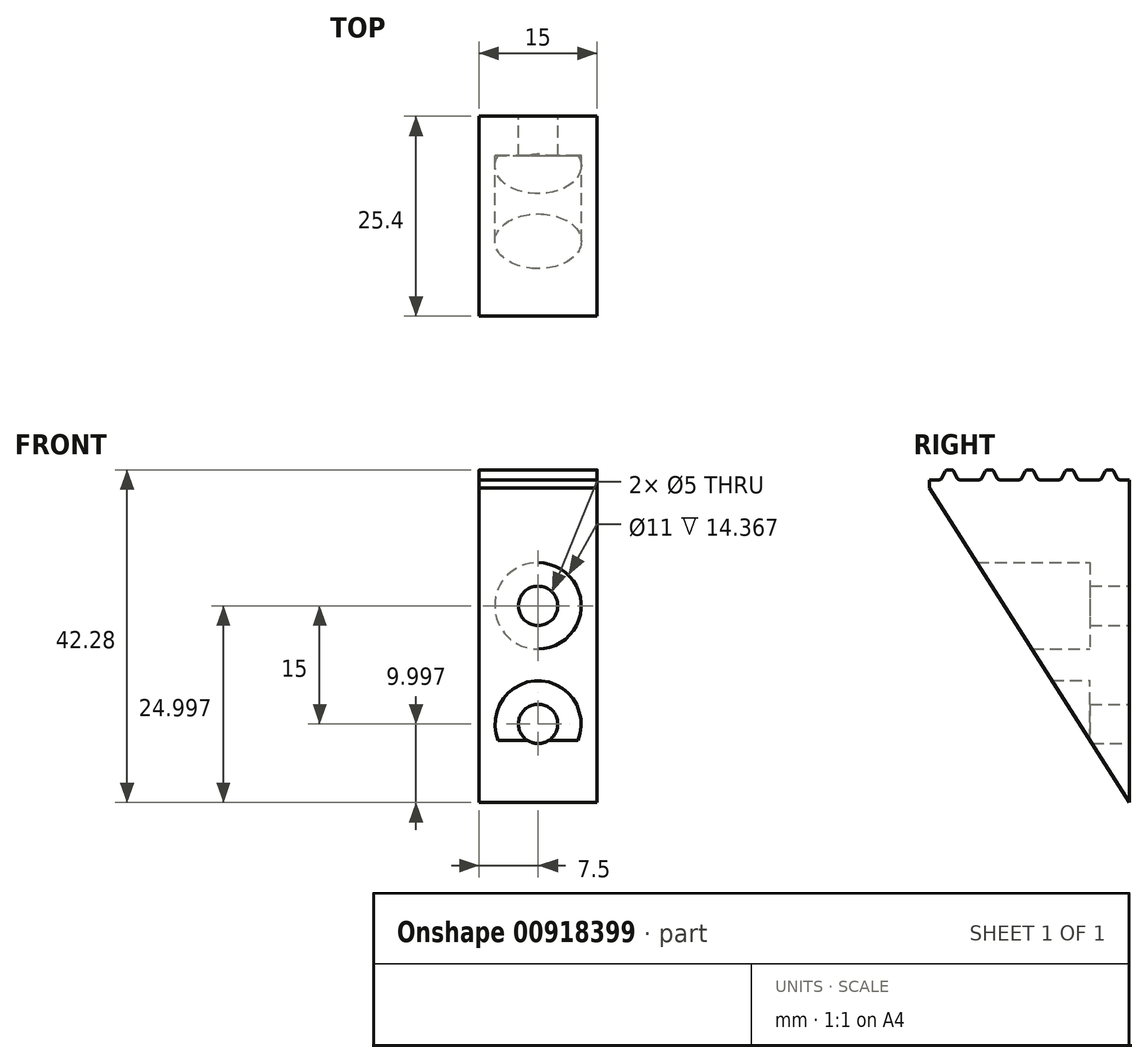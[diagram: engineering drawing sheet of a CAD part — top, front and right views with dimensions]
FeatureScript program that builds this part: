
annotation { "Feature Type Name" : "Feature", "Feature Type Description" : "" }
export const myFeature = defineFeature(function(context is Context, id is Id, definition is map)
    precondition{}
    {
        {
            var Q0;
            Q0=qCreatedBy(makeId("Right.planeOp"),FACE);
            var sketch = newSketch(context, id + "F0", { "sketchPlane" : qUnion([Q0])});
            skArc(sketch, "E0", {"start": v(8.88, -0.13) * mm, "mid": v(9.08, -0.07) * mm, "end": v(9.22, 0.1) * mm});
            skLineSegment(sketch, "E1", {"start": v(9.22, 0.1) * mm, "end": v(9.6, 0.92) * mm});
            skArc(sketch, "E2", {"start": v(9.95, 1.14) * mm, "mid": v(9.75, 1.08) * mm, "end": v(9.6, 0.92) * mm});
            skLineSegment(sketch, "E3", {"start": v(9.95, 1.14) * mm, "end": v(10.37, 1.14) * mm});
            skArc(sketch, "E4", {"start": v(10.7, 0.93) * mm, "mid": v(10.57, 1.08) * mm, "end": v(10.37, 1.14) * mm});
            skLineSegment(sketch, "E5", {"start": v(10.7, 0.93) * mm, "end": v(11.1, 0.1) * mm});
            skArc(sketch, "E6", {"start": v(11.1, 0.1) * mm, "mid": v(11.24, -0.07) * mm, "end": v(11.44, -0.13) * mm});
            skLineSegment(sketch, "E7", {"start": v(11.44, -0.13) * mm, "end": v(12.7, -0.13) * mm});
            skLineSegment(sketch, "E8", {"start": v(12.7, -0.13) * mm, "end": v(12.7, -1.14) * mm});
            skArc(sketch, "E9", {"start": v(3.8, -0.13) * mm, "mid": v(4, -0.07) * mm, "end": v(4.14, 0.1) * mm});
            skLineSegment(sketch, "E10", {"start": v(4.14, 0.1) * mm, "end": v(4.53, 0.92) * mm});
            skArc(sketch, "E11", {"start": v(4.87, 1.14) * mm, "mid": v(4.67, 1.08) * mm, "end": v(4.53, 0.92) * mm});
            skLineSegment(sketch, "E12", {"start": v(4.87, 1.14) * mm, "end": v(5.29, 1.14) * mm});
            skArc(sketch, "E13", {"start": v(5.63, 0.93) * mm, "mid": v(5.49, 1.08) * mm, "end": v(5.29, 1.14) * mm});
            skLineSegment(sketch, "E14", {"start": v(5.63, 0.93) * mm, "end": v(6.02, 0.1) * mm});
            skArc(sketch, "E15", {"start": v(6.02, 0.1) * mm, "mid": v(6.16, -0.07) * mm, "end": v(6.36, -0.13) * mm});
            skLineSegment(sketch, "E16", {"start": v(6.36, -0.13) * mm, "end": v(8.88, -0.13) * mm});
            skArc(sketch, "E17", {"start": v(-1.28, -0.13) * mm, "mid": v(-1.08, -0.07) * mm, "end": v(-0.94, 0.1) * mm});
            skLineSegment(sketch, "E18", {"start": v(-0.94, 0.1) * mm, "end": v(-0.55, 0.92) * mm});
            skArc(sketch, "E19", {"start": v(-0.2, 1.14) * mm, "mid": v(-0.41, 1.08) * mm, "end": v(-0.55, 0.92) * mm});
            skLineSegment(sketch, "E20", {"start": v(-0.2, 1.14) * mm, "end": v(0.2, 1.14) * mm});
            skArc(sketch, "E21", {"start": v(0.55, 0.93) * mm, "mid": v(0.4, 1.08) * mm, "end": v(0.2, 1.14) * mm});
            skLineSegment(sketch, "E22", {"start": v(0.55, 0.93) * mm, "end": v(0.94, 0.1) * mm});
            skArc(sketch, "E23", {"start": v(0.94, 0.1) * mm, "mid": v(1.08, -0.07) * mm, "end": v(1.28, -0.13) * mm});
            skLineSegment(sketch, "E24", {"start": v(1.28, -0.13) * mm, "end": v(3.8, -0.13) * mm});
            skArc(sketch, "E25", {"start": v(-6.36, -0.13) * mm, "mid": v(-6.16, -0.07) * mm, "end": v(-6.02, 0.1) * mm});
            skLineSegment(sketch, "E26", {"start": v(-6.02, 0.1) * mm, "end": v(-5.63, 0.92) * mm});
            skArc(sketch, "E27", {"start": v(-5.29, 1.14) * mm, "mid": v(-5.5, 1.08) * mm, "end": v(-5.63, 0.92) * mm});
            skLineSegment(sketch, "E28", {"start": v(-5.29, 1.14) * mm, "end": v(-4.87, 1.14) * mm});
            skArc(sketch, "E29", {"start": v(-4.53, 0.93) * mm, "mid": v(-4.67, 1.08) * mm, "end": v(-4.87, 1.14) * mm});
            skLineSegment(sketch, "E30", {"start": v(-4.53, 0.93) * mm, "end": v(-4.14, 0.1) * mm});
            skArc(sketch, "E31", {"start": v(-4.14, 0.1) * mm, "mid": v(-4, -0.07) * mm, "end": v(-3.8, -0.13) * mm});
            skLineSegment(sketch, "E32", {"start": v(-3.8, -0.13) * mm, "end": v(-1.28, -0.13) * mm});
            skLineSegment(sketch, "E33", {"start": v(-12.7, -0.13) * mm, "end": v(-11.44, -0.13) * mm});
            skArc(sketch, "E34", {"start": v(-11.44, -0.13) * mm, "mid": v(-11.24, -0.07) * mm, "end": v(-11.1, 0.1) * mm});
            skLineSegment(sketch, "E35", {"start": v(-11.1, 0.1) * mm, "end": v(-10.71, 0.92) * mm});
            skArc(sketch, "E36", {"start": v(-10.37, 1.14) * mm, "mid": v(-10.57, 1.08) * mm, "end": v(-10.71, 0.92) * mm});
            skLineSegment(sketch, "E37", {"start": v(-10.37, 1.14) * mm, "end": v(-9.95, 1.14) * mm});
            skArc(sketch, "E38", {"start": v(-9.61, 0.93) * mm, "mid": v(-9.75, 1.08) * mm, "end": v(-9.95, 1.14) * mm});
            skLineSegment(sketch, "E39", {"start": v(-9.61, 0.93) * mm, "end": v(-9.22, 0.1) * mm});
            skArc(sketch, "E40", {"start": v(-9.22, 0.1) * mm, "mid": v(-9.08, -0.07) * mm, "end": v(-8.88, -0.13) * mm});
            skLineSegment(sketch, "E41", {"start": v(-8.88, -0.13) * mm, "end": v(-6.36, -0.13) * mm});
            skLineSegment(sketch, "E42", {"start": v(12.7, -1.14) * mm, "end": v(-12.7, -1.14) * mm, "construction": true});
            skLineSegment(sketch, "E43", {"start": v(-12.7, -1.14) * mm, "end": v(-12.7, -0.13) * mm});
            skLineSegment(sketch, "E44.right", {"start": v(12.7, -1.14) * mm, "end": v(12.7, -41.14) * mm});
            skLineSegment(sketch, "E45", {"start": v(-12.7, -1.14) * mm, "end": v(12.7, -41.14) * mm});
            skSolve(sketch);
        }
        {
            var Q0;
            Q0=makeQuery(id+"F0.imprint","IMPRINT",FACE,{"disambiguationData":[TD([[makeQuery(id+"F0.imprint","IMPRINT",EDGE,{"derivedFrom":sQuery(id+"F0.wireOp",EDGE,"E0")}),-1.0]])]});
            extrude(context, id + "F1", {"entities" : qUnion([Q0]), "oppositeDirection" : true, "depth" : 7.5 * mm, "offsetDistance" : 25 * mm});
        }
        {
            var Q0;
            Q0=makeQuery(id+"F1.opExtrude","CAP_FACE",FACE,{"disambiguationData":[OSD([sQuery(id+"F0.wireOp",EDGE,"E0"),sQuery(id+"F0.wireOp",EDGE,"E1"),sQuery(id+"F0.wireOp",EDGE,"E2"),sQuery(id+"F0.wireOp",EDGE,"E3"),sQuery(id+"F0.wireOp",EDGE,"E4"),sQuery(id+"F0.wireOp",EDGE,"E5"),sQuery(id+"F0.wireOp",EDGE,"E6"),sQuery(id+"F0.wireOp",EDGE,"E7"),sQuery(id+"F0.wireOp",EDGE,"E8"),sQuery(id+"F0.wireOp",EDGE,"E9"),sQuery(id+"F0.wireOp",EDGE,"E10"),sQuery(id+"F0.wireOp",EDGE,"E11"),sQuery(id+"F0.wireOp",EDGE,"E12"),sQuery(id+"F0.wireOp",EDGE,"E13"),sQuery(id+"F0.wireOp",EDGE,"E14"),sQuery(id+"F0.wireOp",EDGE,"E15"),sQuery(id+"F0.wireOp",EDGE,"E16"),sQuery(id+"F0.wireOp",EDGE,"E17"),sQuery(id+"F0.wireOp",EDGE,"E18"),sQuery(id+"F0.wireOp",EDGE,"E19"),sQuery(id+"F0.wireOp",EDGE,"E20"),sQuery(id+"F0.wireOp",EDGE,"E21"),sQuery(id+"F0.wireOp",EDGE,"E22"),sQuery(id+"F0.wireOp",EDGE,"E23"),sQuery(id+"F0.wireOp",EDGE,"E24"),sQuery(id+"F0.wireOp",EDGE,"E25"),sQuery(id+"F0.wireOp",EDGE,"E26"),sQuery(id+"F0.wireOp",EDGE,"E27"),sQuery(id+"F0.wireOp",EDGE,"E28"),sQuery(id+"F0.wireOp",EDGE,"E29"),sQuery(id+"F0.wireOp",EDGE,"E30"),sQuery(id+"F0.wireOp",EDGE,"E31"),sQuery(id+"F0.wireOp",EDGE,"E32"),sQuery(id+"F0.wireOp",EDGE,"E33"),sQuery(id+"F0.wireOp",EDGE,"E34"),sQuery(id+"F0.wireOp",EDGE,"E35"),sQuery(id+"F0.wireOp",EDGE,"E36"),sQuery(id+"F0.wireOp",EDGE,"E37"),sQuery(id+"F0.wireOp",EDGE,"E38"),sQuery(id+"F0.wireOp",EDGE,"E39"),sQuery(id+"F0.wireOp",EDGE,"E40"),sQuery(id+"F0.wireOp",EDGE,"E41"),sQuery(id+"F0.wireOp",EDGE,"E43"),sQuery(id+"F0.wireOp",EDGE,"E44.right"),sQuery(id+"F0.wireOp",EDGE,"E45")])],"isStart":false});
            var sketch = newSketch(context, id + "F2", { "sketchPlane" : qUnion([Q0])});
            skLineSegment(sketch, "E46", {"start": v(-12.7, -0.13) * mm, "end": v(12.7, -0.13) * mm});
            skSolve(sketch);
        }
        {
            var Q0;
            Q0=makeQuery(id+"F1.opExtrude","SWEPT_BODY",BODY,{"disambiguationData":[OSD([sQuery(id+"F0.wireOp",EDGE,"E0"),sQuery(id+"F0.wireOp",EDGE,"E1"),sQuery(id+"F0.wireOp",EDGE,"E2"),sQuery(id+"F0.wireOp",EDGE,"E3"),sQuery(id+"F0.wireOp",EDGE,"E4"),sQuery(id+"F0.wireOp",EDGE,"E5"),sQuery(id+"F0.wireOp",EDGE,"E6"),sQuery(id+"F0.wireOp",EDGE,"E7"),sQuery(id+"F0.wireOp",EDGE,"E8"),sQuery(id+"F0.wireOp",EDGE,"E9"),sQuery(id+"F0.wireOp",EDGE,"E10"),sQuery(id+"F0.wireOp",EDGE,"E11"),sQuery(id+"F0.wireOp",EDGE,"E12"),sQuery(id+"F0.wireOp",EDGE,"E13"),sQuery(id+"F0.wireOp",EDGE,"E14"),sQuery(id+"F0.wireOp",EDGE,"E15"),sQuery(id+"F0.wireOp",EDGE,"E16"),sQuery(id+"F0.wireOp",EDGE,"E17"),sQuery(id+"F0.wireOp",EDGE,"E18"),sQuery(id+"F0.wireOp",EDGE,"E19"),sQuery(id+"F0.wireOp",EDGE,"E20"),sQuery(id+"F0.wireOp",EDGE,"E21"),sQuery(id+"F0.wireOp",EDGE,"E22"),sQuery(id+"F0.wireOp",EDGE,"E23"),sQuery(id+"F0.wireOp",EDGE,"E24"),sQuery(id+"F0.wireOp",EDGE,"E25"),sQuery(id+"F0.wireOp",EDGE,"E26"),sQuery(id+"F0.wireOp",EDGE,"E27"),sQuery(id+"F0.wireOp",EDGE,"E28"),sQuery(id+"F0.wireOp",EDGE,"E29"),sQuery(id+"F0.wireOp",EDGE,"E30"),sQuery(id+"F0.wireOp",EDGE,"E31"),sQuery(id+"F0.wireOp",EDGE,"E32"),sQuery(id+"F0.wireOp",EDGE,"E33"),sQuery(id+"F0.wireOp",EDGE,"E34"),sQuery(id+"F0.wireOp",EDGE,"E35"),sQuery(id+"F0.wireOp",EDGE,"E36"),sQuery(id+"F0.wireOp",EDGE,"E37"),sQuery(id+"F0.wireOp",EDGE,"E38"),sQuery(id+"F0.wireOp",EDGE,"E39"),sQuery(id+"F0.wireOp",EDGE,"E40"),sQuery(id+"F0.wireOp",EDGE,"E41"),sQuery(id+"F0.wireOp",EDGE,"E43"),sQuery(id+"F0.wireOp",EDGE,"E44.right"),sQuery(id+"F0.wireOp",EDGE,"E45")])]});
            var Q1;
            Q1=qCreatedBy(makeId("Right.planeOp"),FACE);
            mirror(context, id + "F4", {"operationType" : NewBodyOperationType.ADD, "entities" : qUnion([Q0]), "mirrorPlane" : qUnion([Q1])});
        }
        {
            var Q0;
            {var subQ0=makeQuery(id+"F3.boolean.opBoolean","MERGE",FACE,{"derivedFrom":[makeQuery(id+"F1.opExtrude","SWEPT_FACE",FACE,{"disambiguationData":[OSD([sQuery(id+"F0.wireOp",EDGE,"E7")])]}),makeQuery(id+"F1.opExtrude","SWEPT_FACE",FACE,{"disambiguationData":[OSD([sQuery(id+"F0.wireOp",EDGE,"E16")])]}),makeQuery(id+"F1.opExtrude","SWEPT_FACE",FACE,{"disambiguationData":[OSD([sQuery(id+"F0.wireOp",EDGE,"E24")])]}),makeQuery(id+"F1.opExtrude","SWEPT_FACE",FACE,{"disambiguationData":[OSD([sQuery(id+"F0.wireOp",EDGE,"E32")])]}),makeQuery(id+"F1.opExtrude","SWEPT_FACE",FACE,{"disambiguationData":[OSD([sQuery(id+"F0.wireOp",EDGE,"E33")])]}),makeQuery(id+"F1.opExtrude","SWEPT_FACE",FACE,{"disambiguationData":[OSD([sQuery(id+"F0.wireOp",EDGE,"E41")])]}),makeQuery(id+"F3.opExtrude","SWEPT_FACE",FACE,{"disambiguationData":[OSD([sQuery(id+"F2.wireOp",EDGE,"E46")])]})]});Q0=makeQuery(id+"F4.boolean.opBoolean","MERGE",FACE,{"derivedFrom":[subQ0,makeQuery(id+"F4.opPattern","COPY",FACE,{"derivedFrom":subQ0,"instanceName":"1"})]});}
            var sketch = newSketch(context, id + "F5", { "sketchPlane" : qUnion([Q0])});
            skCircle(sketch, "E47", {"center": v(10, 7.7) * mm, "radius": 0.8 * mm});
            skCircle(sketch, "E48", {"center": v(10, -7.7) * mm, "radius": 0.8 * mm});
            skCircle(sketch, "E49.MirrorC", {"center": v(-10, 7.7) * mm, "radius": 0.8 * mm});
            skCircle(sketch, "E50.MirrorC", {"center": v(-10, -7.7) * mm, "radius": 0.8 * mm});
            skSolve(sketch);
        }
        {
            var Q0;
            Q0=qSketchRegion(id+"F5",true);
            extrude(context, id + "F6", {"entities" : qUnion([Q0]), "operationType" : NewBodyOperationType.REMOVE, "oppositeDirection" : true, "depth" : 45 * mm, "offsetDistance" : 25 * mm});
        }
        {
            var Q0;
            {var subQ0=makeQuery(id+"F3.boolean.opBoolean","MERGE",FACE,{"derivedFrom":[makeQuery(id+"F1.opExtrude","SWEPT_FACE",FACE,{"disambiguationData":[OSD([sQuery(id+"F0.wireOp",EDGE,"E7")])]}),makeQuery(id+"F1.opExtrude","SWEPT_FACE",FACE,{"disambiguationData":[OSD([sQuery(id+"F0.wireOp",EDGE,"E16")])]}),makeQuery(id+"F1.opExtrude","SWEPT_FACE",FACE,{"disambiguationData":[OSD([sQuery(id+"F0.wireOp",EDGE,"E24")])]}),makeQuery(id+"F1.opExtrude","SWEPT_FACE",FACE,{"disambiguationData":[OSD([sQuery(id+"F0.wireOp",EDGE,"E32")])]}),makeQuery(id+"F1.opExtrude","SWEPT_FACE",FACE,{"disambiguationData":[OSD([sQuery(id+"F0.wireOp",EDGE,"E33")])]}),makeQuery(id+"F1.opExtrude","SWEPT_FACE",FACE,{"disambiguationData":[OSD([sQuery(id+"F0.wireOp",EDGE,"E41")])]}),makeQuery(id+"F3.opExtrude","SWEPT_FACE",FACE,{"disambiguationData":[OSD([sQuery(id+"F2.wireOp",EDGE,"E46")])]})]});Q0=makeQuery(id+"F4.boolean.opBoolean","MERGE",FACE,{"derivedFrom":[subQ0,makeQuery(id+"F4.opPattern","COPY",FACE,{"derivedFrom":subQ0,"instanceName":"1"})]});}
            var sketch = newSketch(context, id + "F7", { "sketchPlane" : qUnion([Q0])});
            skCircle(sketch, "E51.0", {"center": v(10, -7.7) * mm, "radius": 2 * mm});
            skCircle(sketch, "E52.0", {"center": v(10, 7.7) * mm, "radius": 2 * mm});
            skCircle(sketch, "E53.MirrorC", {"center": v(-10, 7.7) * mm, "radius": 2 * mm});
            skCircle(sketch, "E54.MirrorC", {"center": v(-10, -7.7) * mm, "radius": 2 * mm});
            skSolve(sketch);
        }
        {
            var Q0;
            Q0=qSketchRegion(id+"F7",true);
            var Q1;
            {var subQ0=sQuery(id+"F0.wireOp",EDGE,"E45");var subQ1=makeQuery(id+"F3.boolean.opBoolean","MERGE",FACE,{"derivedFrom":[makeQuery(id+"F1.opExtrude","SWEPT_FACE",FACE,{"disambiguationData":[OSD([subQ0])]}),makeQuery(id+"F3.opExtrude","SWEPT_FACE",FACE,{"disambiguationData":[OSD([subQ0])]})]});Q1=makeQuery(id+"F4.boolean.opBoolean","MERGE",FACE,{"derivedFrom":[subQ1,makeQuery(id+"F4.opPattern","COPY",FACE,{"derivedFrom":subQ1,"instanceName":"1"})]});}
            extrude(context, id + "F8", {"entities" : qUnion([Q0]), "operationType" : NewBodyOperationType.REMOVE, "endBound" : BoundingType.UP_TO_SURFACE, "oppositeDirection" : true, "depth" : 40 * mm, "endBoundEntityFace" : qUnion([Q1]), "offsetDistance" : 3 * mm, "hasSecondDirection" : true, "secondDirectionOppositeDirection" : true, "secondDirectionDepth" : 3 * mm});
        }
        {
            var Q0;
            {var subQ0=sQuery(id+"F0.wireOp",EDGE,"E44.right");var subQ1=sQuery(id+"F0.wireOp",EDGE,"E8");var subQ2=makeQuery(id+"F3.boolean.opBoolean","MERGE",FACE,{"derivedFrom":[makeQuery(id+"F1.opExtrude","SWEPT_FACE",FACE,{"disambiguationData":[OSD([subQ1,subQ0])]}),makeQuery(id+"F3.opExtrude","SWEPT_FACE",FACE,{"disambiguationData":[OSD([subQ1,subQ0])]})]});Q0=makeQuery(id+"F4.boolean.opBoolean","MERGE",FACE,{"derivedFrom":[subQ2,makeQuery(id+"F4.opPattern","COPY",FACE,{"derivedFrom":subQ2,"instanceName":"1"})]});}
            var sketch = newSketch(context, id + "F9", { "sketchPlane" : qUnion([Q0])});
            skCircle(sketch, "E55", {"center": v(0, -31.14) * mm, "radius": 2.5 * mm});
            skCircle(sketch, "E56", {"center": v(0, -16.14) * mm, "radius": 2.5 * mm});
            skSolve(sketch);
        }
        {
            var Q0;
            Q0=makeQuery(id+"F9.imprint","IMPRINT",FACE,{"disambiguationData":[TD([[makeQuery(id+"F9.imprint","IMPRINT",EDGE,{"derivedFrom":sQuery(id+"F9.wireOp",EDGE,"E55")}),1.0]])]});
            var Q1;
            Q1=makeQuery(id+"F9.imprint","IMPRINT",FACE,{"disambiguationData":[TD([[makeQuery(id+"F9.imprint","IMPRINT",EDGE,{"derivedFrom":sQuery(id+"F9.wireOp",EDGE,"E56")}),1.0]])]});
            var Q2;
            {var subQ0=sQuery(id+"F0.wireOp",EDGE,"E45");var subQ1=makeQuery(id+"F3.boolean.opBoolean","MERGE",FACE,{"derivedFrom":[makeQuery(id+"F1.opExtrude","SWEPT_FACE",FACE,{"disambiguationData":[OSD([subQ0])]}),makeQuery(id+"F3.opExtrude","SWEPT_FACE",FACE,{"disambiguationData":[OSD([subQ0])]})]});Q2=makeQuery(id+"F4.boolean.opBoolean","MERGE",FACE,{"derivedFrom":[subQ1,makeQuery(id+"F4.opPattern","COPY",FACE,{"derivedFrom":subQ1,"instanceName":"1"})]});}
            extrude(context, id + "F10", {"entities" : qUnion([Q0, Q1]), "operationType" : NewBodyOperationType.REMOVE, "endBound" : BoundingType.UP_TO_SURFACE, "oppositeDirection" : true, "depth" : 25 * mm, "endBoundEntityFace" : qUnion([Q2]), "offsetDistance" : 25 * mm});
        }
        {
            var Q0;
            {var subQ0=sQuery(id+"F0.wireOp",EDGE,"E44.right");var subQ1=sQuery(id+"F0.wireOp",EDGE,"E8");var subQ2=makeQuery(id+"F3.boolean.opBoolean","MERGE",FACE,{"derivedFrom":[makeQuery(id+"F1.opExtrude","SWEPT_FACE",FACE,{"disambiguationData":[OSD([subQ1,subQ0])]}),makeQuery(id+"F3.opExtrude","SWEPT_FACE",FACE,{"disambiguationData":[OSD([subQ1,subQ0])]})]});Q0=makeQuery(id+"F4.boolean.opBoolean","MERGE",FACE,{"derivedFrom":[subQ2,makeQuery(id+"F4.opPattern","COPY",FACE,{"derivedFrom":subQ2,"instanceName":"1"})]});}
            var sketch = newSketch(context, id + "F11", { "sketchPlane" : qUnion([Q0])});
            skCircle(sketch, "E57.0", {"center": v(0, -31.14) * mm, "radius": 5.5 * mm});
            skCircle(sketch, "E58.0", {"center": v(0, -16.14) * mm, "radius": 5.5 * mm});
            skSolve(sketch);
        }
        {
            var Q0;
            Q0=qSketchRegion(id+"F11",true);
            var Q1;
            {var subQ0=sQuery(id+"F0.wireOp",EDGE,"E45");var subQ1=makeQuery(id+"F3.boolean.opBoolean","MERGE",FACE,{"derivedFrom":[makeQuery(id+"F1.opExtrude","SWEPT_FACE",FACE,{"disambiguationData":[OSD([subQ0])]}),makeQuery(id+"F3.opExtrude","SWEPT_FACE",FACE,{"disambiguationData":[OSD([subQ0])]})]});Q1=makeQuery(id+"F4.boolean.opBoolean","MERGE",FACE,{"derivedFrom":[subQ1,makeQuery(id+"F4.opPattern","COPY",FACE,{"derivedFrom":subQ1,"instanceName":"1"})]});}
            extrude(context, id + "F12", {"entities" : qUnion([Q0]), "operationType" : NewBodyOperationType.REMOVE, "endBound" : BoundingType.UP_TO_SURFACE, "oppositeDirection" : true, "depth" : 25 * mm, "endBoundEntityFace" : qUnion([Q1]), "offsetDistance" : 25 * mm, "hasSecondDirection" : true, "secondDirectionOppositeDirection" : true, "secondDirectionDepth" : 5 * mm});
        }
    });
